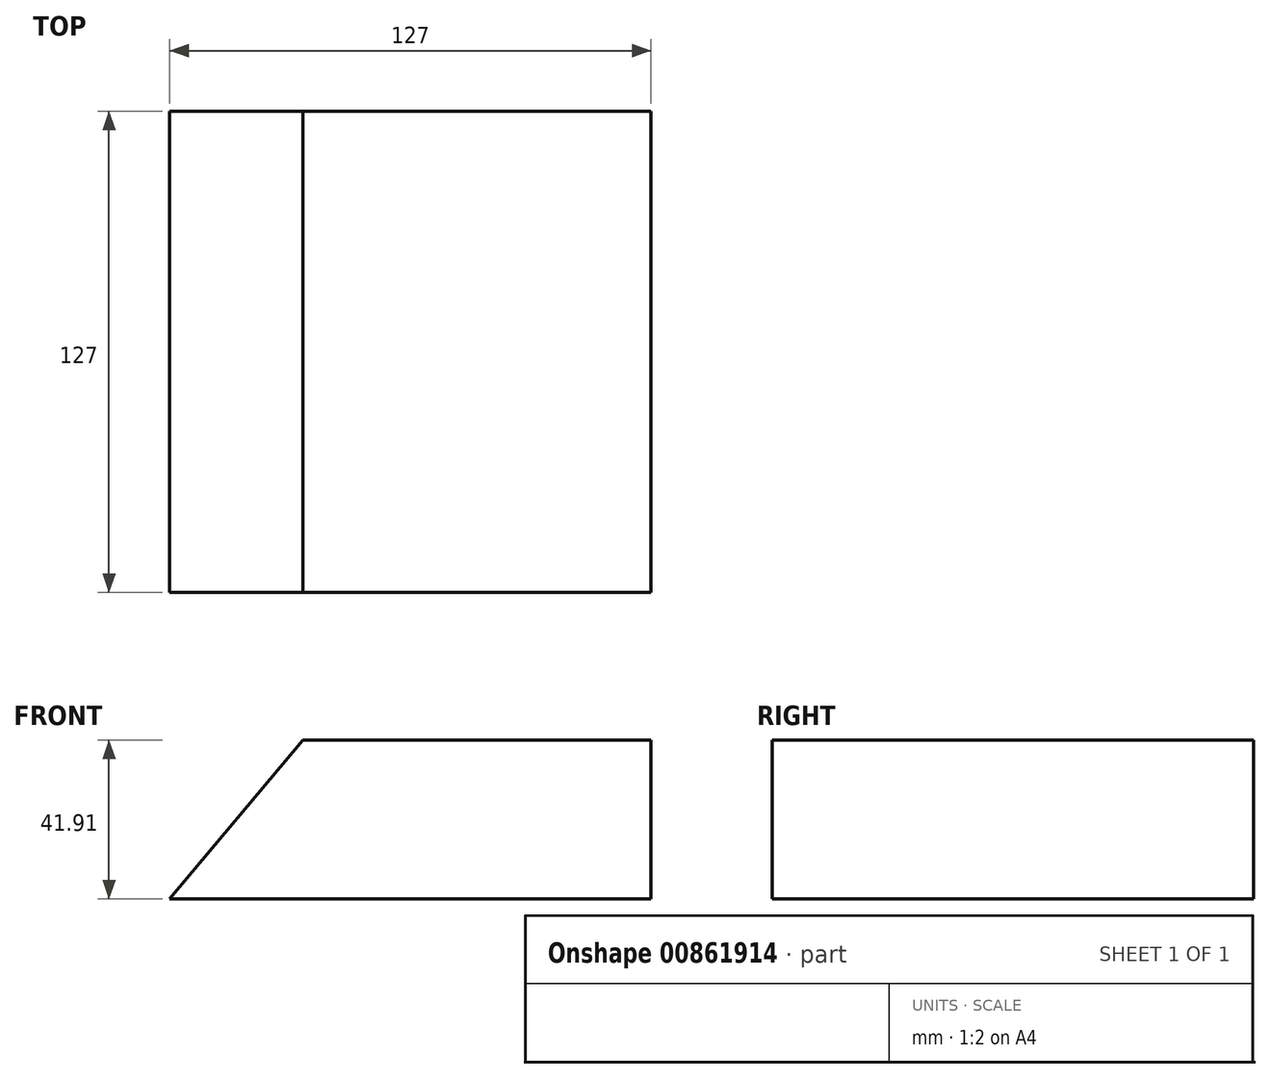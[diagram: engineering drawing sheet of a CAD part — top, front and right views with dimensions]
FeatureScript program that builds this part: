
annotation { "Feature Type Name" : "Feature", "Feature Type Description" : "" }
export const myFeature = defineFeature(function(context is Context, id is Id, definition is map)
    precondition{}
    {
        {
            var Q0;
            Q0=qCreatedBy(makeId("Front.planeOp"),FACE);
            var sketch = newSketch(context, id + "F0", { "sketchPlane" : qUnion([Q0])});
            skLineSegment(sketch, "E0", {"start": v(-142.68, 0) * mm, "end": v(-15.68, 0) * mm});
            skLineSegment(sketch, "E1", {"start": v(-15.68, 0) * mm, "end": v(-15.68, 41.91) * mm});
            skLineSegment(sketch, "E2", {"start": v(-15.68, 41.91) * mm, "end": v(-107.51, 41.91) * mm});
            skLineSegment(sketch, "E3", {"start": v(-107.51, 41.91) * mm, "end": v(-142.68, 0) * mm});
            skSolve(sketch);
        }
        {
            var Q0;
            Q0=makeQuery(id+"F0.imprint","IMPRINT",FACE,{"disambiguationData":[TD([[makeQuery(id+"F0.imprint","IMPRINT",EDGE,{"derivedFrom":sQuery(id+"F0.wireOp",EDGE,"E0")}),1.0]])]});
            extrude(context, id + "F1", {"entities" : qUnion([Q0]), "depth" : 127 * mm, "offsetDistance" : 25.4 * mm});
        }
    });
